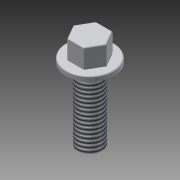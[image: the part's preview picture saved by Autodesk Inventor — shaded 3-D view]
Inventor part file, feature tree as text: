
AUTODESK INVENTOR PART (.ipt)
format: ipt  version: 2015 (Build 190159000, 159)  size: 132,608 bytes
history: native  units: mm
features: extrude x3, sketch x3, fillet x1, thread x1, chamfer x1
ambient origin geometry x8: Origin, YZ Plane, XZ Plane, XY Plane, X Axis, Y Axis, Z Axis, Center Point
bodies: 实体1 (feature_tree)
feature tree (9):
  extrude  "拉伸1"  Depth=5.0mm TaperAngle=0.0deg
  extrude  "拉伸2"  Depth=6.0mm
  fillet  "圆角1"  Radius=4.0mm
  extrude  "拉伸3"  Depth=5.0mm
  thread  "螺纹1"  [1 undecoded]
  chamfer  "倒角1"  Distance=10.0mm
  sketch  "草图1"  dims[d0=10.0mm d1=5.0mm d2=0.0mm]
  sketch  "草图2"  dims[d3=1.036718mm d4=6.0mm d5=4.0mm d6=0.0mm]
  sketch  "草图3"  dims[d7=0.25mm d8=5.0mm d9=15.0mm d10=0.0mm d11=10.0mm d12=0.0mm d13=0.225mm d14=2.0mm d15=45.0deg]
note: 1 required parameter value undecoded (feature->parameter linkage not recoverable at this tier; creation-order binding heuristic only, values carry confidence <= 0.55)
